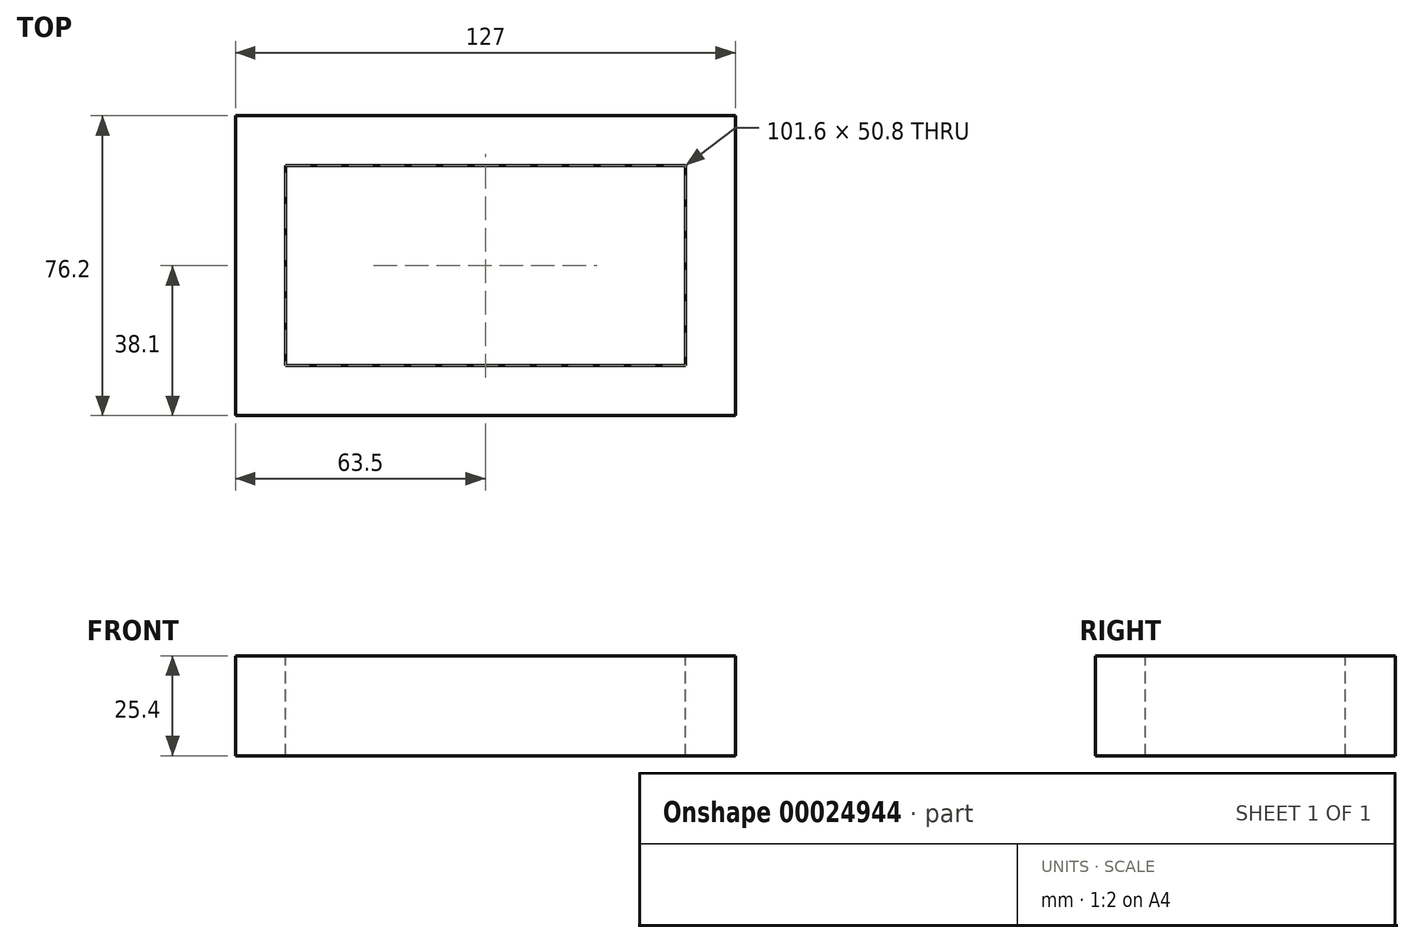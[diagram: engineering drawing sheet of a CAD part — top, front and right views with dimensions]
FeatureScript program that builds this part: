
annotation { "Feature Type Name" : "Feature", "Feature Type Description" : "" }
export const myFeature = defineFeature(function(context is Context, id is Id, definition is map)
    precondition{}
    {
        {
            var Q0;
            Q0=qCreatedBy(makeId("Top.planeOp"),FACE);
            var sketch = newSketch(context, id + "F0", { "sketchPlane" : qUnion([Q0])});
            skLineSegment(sketch, "E0.rect.bottom", {"start": v(-63.5, 38.1) * mm, "end": v(63.5, 38.1) * mm});
            skLineSegment(sketch, "E0.rect.top", {"start": v(-63.5, -38.1) * mm, "end": v(63.5, -38.1) * mm});
            skLineSegment(sketch, "E0.rect.left", {"start": v(-63.5, 38.1) * mm, "end": v(-63.5, -38.1) * mm});
            skLineSegment(sketch, "E0.rect.right", {"start": v(63.5, 38.1) * mm, "end": v(63.5, -38.1) * mm});
            skPoint(sketch, "E0.rect.middle", {"position": v(0, 0) * mm});
            skSolve(sketch);
        }
        {
            var Q0;
            Q0 = qSketchRegion(id + "F0", true);
            extrude(context, id + "F1", {"entities" : qUnion([Q0]), "endBound" : BoundingType.SYMMETRIC, "depth" : 25.4 * mm});
        }
        {
            var Q0;
            Q0=makeQuery(id+"F1.opExtrude","CAP_FACE",FACE,{"disambiguationData":[OSD([sQuery(id+"F0.wireOp",EDGE,"E0.rect.bottom"),sQuery(id+"F0.wireOp",EDGE,"E0.rect.top"),sQuery(id+"F0.wireOp",EDGE,"E0.rect.left"),sQuery(id+"F0.wireOp",EDGE,"E0.rect.right")])],"isStart":false});
            var sketch = newSketch(context, id + "F2", { "sketchPlane" : qUnion([Q0])});
            skLineSegment(sketch, "E1.rect.bottom", {"start": v(-50.8, 25.4) * mm, "end": v(50.8, 25.4) * mm});
            skLineSegment(sketch, "E1.rect.top", {"start": v(-50.8, -25.4) * mm, "end": v(50.8, -25.4) * mm});
            skLineSegment(sketch, "E1.rect.left", {"start": v(-50.8, 25.4) * mm, "end": v(-50.8, -25.4) * mm});
            skLineSegment(sketch, "E1.rect.right", {"start": v(50.8, 25.4) * mm, "end": v(50.8, -25.4) * mm});
            skPoint(sketch, "E1.rect.middle", {"position": v(0, 0) * mm});
            skLineSegment(sketch, "E2.rect.bottom", {"start": v(-63.5, 25.4) * mm, "end": v(-38.1, 25.4) * mm, "construction": true});
            skLineSegment(sketch, "E2.rect.top", {"start": v(-63.5, 25.4) * mm, "end": v(-38.1, 25.4) * mm, "construction": true});
            skLineSegment(sketch, "E2.rect.left", {"start": v(-63.5, 25.4) * mm, "end": v(-63.5, 25.4) * mm});
            skLineSegment(sketch, "E2.rect.right", {"start": v(-38.1, 25.4) * mm, "end": v(-38.1, 25.4) * mm});
            skPoint(sketch, "E2.rect.middle", {"position": v(-50.8, 25.4) * mm});
            skLineSegment(sketch, "E3.rect.bottom", {"start": v(-50.8, 38.1) * mm, "end": v(-50.8, 38.1) * mm});
            skLineSegment(sketch, "E3.rect.top", {"start": v(-50.8, 12.7) * mm, "end": v(-50.8, 12.7) * mm});
            skLineSegment(sketch, "E3.rect.left", {"start": v(-50.8, 38.1) * mm, "end": v(-50.8, 12.7) * mm, "construction": true});
            skLineSegment(sketch, "E3.rect.right", {"start": v(-50.8, 38.1) * mm, "end": v(-50.8, 12.7) * mm, "construction": true});
            skSolve(sketch);
        }
        {
            var Q0;
            Q0 = qSketchRegion(id + "F2", true);
            extrude(context, id + "F3", {"entities" : qUnion([Q0]), "operationType" : NewBodyOperationType.REMOVE, "endBound" : BoundingType.THROUGH_ALL, "oppositeDirection" : true, "depth" : 25.4 * mm});
        }
    });
